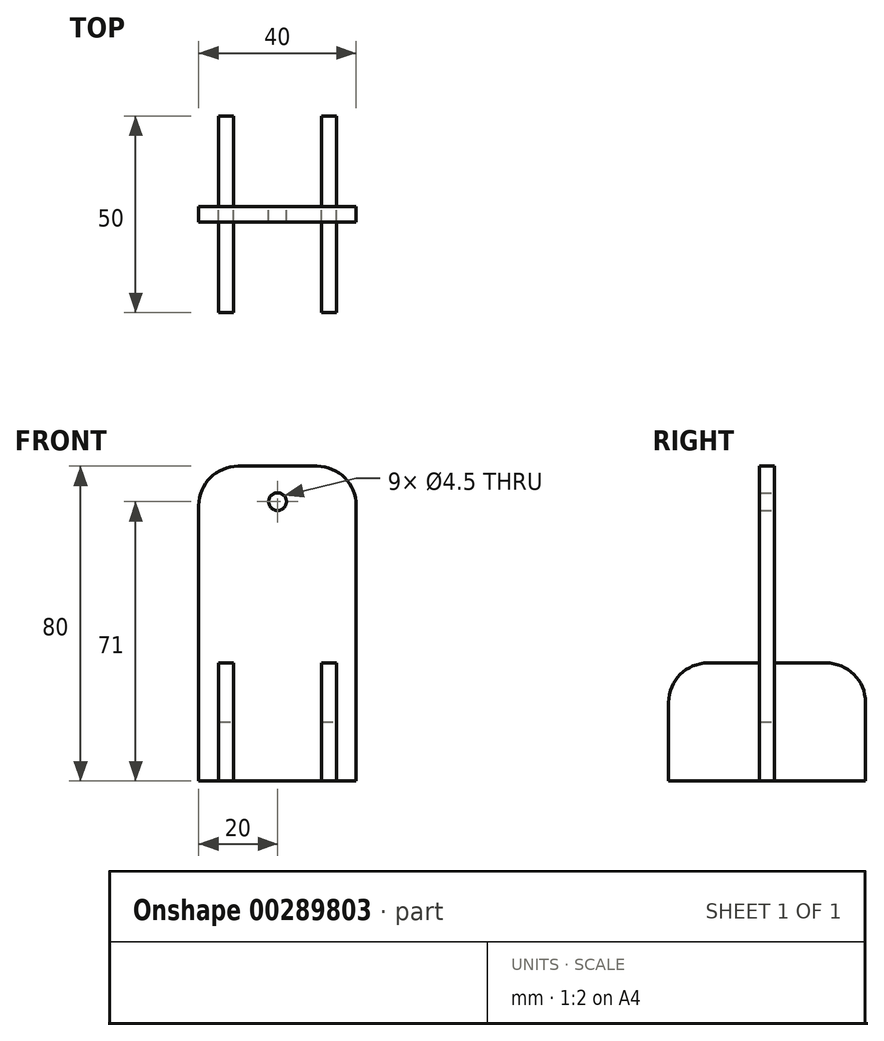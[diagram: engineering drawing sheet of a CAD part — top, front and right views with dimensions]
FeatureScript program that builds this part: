
annotation { "Feature Type Name" : "Feature", "Feature Type Description" : "" }
export const myFeature = defineFeature(function(context is Context, id is Id, definition is map)
    precondition{}
    {
        {
            var Q0;
            Q0=qCreatedBy(makeId("Front.planeOp"),FACE);
            var sketch = newSketch(context, id + "F0", { "sketchPlane" : qUnion([Q0])});
            skLineSegment(sketch, "E0.bottom", {"start": v(20, -40) * mm, "end": v(15, -40) * mm});
            skLineSegment(sketch, "E0.top", {"start": v(10, 40) * mm, "end": v(-10, 40) * mm});
            skLineSegment(sketch, "E0.left", {"start": v(20, -40) * mm, "end": v(20, 30) * mm});
            skLineSegment(sketch, "E0.right", {"start": v(-20, -40) * mm, "end": v(-20, 30) * mm});
            skPoint(sketch, "E0.middle", {"position": v(0, 0) * mm});
            skLineSegment(sketch, "E1", {"start": v(-15, -40) * mm, "end": v(-15, -25) * mm});
            skLineSegment(sketch, "E2", {"start": v(-15, -25) * mm, "end": v(-11.15, -25) * mm});
            skLineSegment(sketch, "E3", {"start": v(-11.15, -25) * mm, "end": v(-11.15, -40) * mm});
            skLineSegment(sketch, "E4", {"start": v(-11.15, -40) * mm, "end": v(11.15, -40) * mm});
            skLineSegment(sketch, "E5", {"start": v(11.15, -40) * mm, "end": v(11.15, -25) * mm});
            skLineSegment(sketch, "E6", {"start": v(11.15, -25) * mm, "end": v(15, -25) * mm});
            skLineSegment(sketch, "E7", {"start": v(15, -25) * mm, "end": v(15, -40) * mm});
            skLineSegment(sketch, "E8.trimOffspring", {"start": v(11.15, -40) * mm, "end": v(-11.15, -40) * mm});
            skLineSegment(sketch, "E9.trimOffspring", {"start": v(-15, -40) * mm, "end": v(-20, -40) * mm});
            skPoint(sketch, "E10.visualSharp", {"position": v(20, 40) * mm});
            skArc(sketch, "E10.filletArc", {"start": v(20, 30) * mm, "mid": v(17.07, 37.07) * mm, "end": v(10, 40) * mm});
            skPoint(sketch, "E11.visualSharp", {"position": v(-20, 40) * mm});
            skArc(sketch, "E11.filletArc", {"start": v(-10, 40) * mm, "mid": v(-17.07, 37.07) * mm, "end": v(-20, 30) * mm});
            skPoint(sketch, "E12", {"position": v(0, 40) * mm});
            skLineSegment(sketch, "E13", {"start": v(0, 40) * mm, "end": v(0, 31) * mm, "construction": true});
            skCircle(sketch, "E14", {"center": v(0, 31) * mm, "radius": 2.25 * mm});
            skSolve(sketch);
        }
        {
            var Q0;
            Q0 = qSketchRegion(id + "F0", true);
            extrude(context, id + "F1", {"entities" : qUnion([Q0]), "endBound" : BoundingType.SYMMETRIC, "depth" : 3.85 * mm});
        }
        {
            var Q0;
            Q0=qCreatedBy(makeId("Right.planeOp"),FACE);
            var sketch = newSketch(context, id + "F2", { "sketchPlane" : qUnion([Q0])});
            skPoint(sketch, "E15.0", {"position": v(0, -25) * mm});
            skLineSegment(sketch, "E16.bottom", {"start": v(-15, -10) * mm, "end": v(-1.92, -10) * mm});
            skLineSegment(sketch, "E16.top", {"start": v(-25, -40) * mm, "end": v(-1.93, -40) * mm});
            skLineSegment(sketch, "E16.left", {"start": v(-25, -20) * mm, "end": v(-25, -40) * mm});
            skLineSegment(sketch, "E16.right", {"start": v(25, -20) * mm, "end": v(25, -40) * mm});
            skPoint(sketch, "E17.visualSharp", {"position": v(25, -10) * mm});
            skArc(sketch, "E17.filletArc", {"start": v(25, -20) * mm, "mid": v(22.07, -12.93) * mm, "end": v(15, -10) * mm});
            skPoint(sketch, "E18.visualSharp", {"position": v(-25, -10) * mm});
            skArc(sketch, "E18.filletArc", {"start": v(-15, -10) * mm, "mid": v(-22.07, -12.93) * mm, "end": v(-25, -20) * mm});
            skPoint(sketch, "E19.0.11.end.orphan", {"position": v(0, -40) * mm});
            skPoint(sketch, "E19.0.7.start.orphan", {"position": v(0, 30) * mm});
            skPoint(sketch, "E19.0.5.start.orphan", {"position": v(0, -40) * mm});
            skPoint(sketch, "E19.0.9.start.orphan", {"position": v(0, -40) * mm});
            skPoint(sketch, "E19.0.3.end.orphan", {"position": v(0, -40) * mm});
            skPoint(sketch, "E19.0.1.start.orphan", {"position": v(0, -40) * mm});
            skLineSegment(sketch, "E20.0.0", {"start": v(1.93, -10) * mm, "end": v(1.93, -25) * mm});
            skLineSegment(sketch, "E20.0.1", {"start": v(1.93, -40) * mm, "end": v(-1.93, -40) * mm});
            skLineSegment(sketch, "E20.0.2", {"start": v(-1.93, -25) * mm, "end": v(-1.93, -10) * mm});
            skLineSegment(sketch, "E20.0.3", {"start": v(-1.93, 30) * mm, "end": v(1.92, 30) * mm});
            skLineSegment(sketch, "E21.0", {"start": v(-1.93, -25) * mm, "end": v(1.92, -25) * mm});
            skLineSegment(sketch, "E22.trimOffspring", {"start": v(1.93, -40) * mm, "end": v(25, -40) * mm});
            skLineSegment(sketch, "E23.trimOffspring", {"start": v(1.92, -10) * mm, "end": v(15, -10) * mm});
            skSolve(sketch);
        }
        {
            var Q0;
            Q0=makeQuery(id+"F1.opExtrude","SWEPT_FACE",FACE,{"disambiguationData":[OSD([sQuery(id+"F0.wireOp",EDGE,"E3")])]});
            var sketch = newSketch(context, id + "F3", { "sketchPlane" : qUnion([Q0])});
            skLineSegment(sketch, "E24.0.0", {"start": v(-25, -40) * mm, "end": v(-25, -20) * mm});
            skArc(sketch, "E24.0.1", {"start": v(-25, -20) * mm, "mid": v(-22.07, -12.93) * mm, "end": v(-15, -10) * mm});
            skLineSegment(sketch, "E24.0.2", {"start": v(-15, -10) * mm, "end": v(-1.92, -10) * mm});
            skLineSegment(sketch, "E24.0.3", {"start": v(-1.93, -10) * mm, "end": v(-1.93, -25) * mm});
            skLineSegment(sketch, "E24.0.4", {"start": v(-1.93, -25) * mm, "end": v(1.93, -25) * mm});
            skLineSegment(sketch, "E24.0.5", {"start": v(1.93, -25) * mm, "end": v(1.93, -10) * mm});
            skLineSegment(sketch, "E24.0.6", {"start": v(1.92, -10) * mm, "end": v(15, -10) * mm});
            skArc(sketch, "E24.0.7", {"start": v(15, -10) * mm, "mid": v(22.07, -12.93) * mm, "end": v(25, -20) * mm});
            skLineSegment(sketch, "E24.0.8", {"start": v(25, -20) * mm, "end": v(25, -40) * mm});
            skLineSegment(sketch, "E24.0.9", {"start": v(25, -40) * mm, "end": v(1.93, -40) * mm});
            skLineSegment(sketch, "E24.0.10", {"start": v(1.93, -40) * mm, "end": v(-1.93, -40) * mm});
            skLineSegment(sketch, "E24.0.11", {"start": v(-1.93, -40) * mm, "end": v(-25, -40) * mm});
            skSolve(sketch);
        }
        {
            var Q0;
            Q0=makeQuery(id+"F1.opExtrude","SWEPT_FACE",FACE,{"disambiguationData":[OSD([sQuery(id+"F0.wireOp",EDGE,"E5")])]});
            var sketch = newSketch(context, id + "F4", { "sketchPlane" : qUnion([Q0])});
            skLineSegment(sketch, "E25.0.0", {"start": v(25, -40) * mm, "end": v(25, -20) * mm});
            skArc(sketch, "E25.0.1", {"start": v(25, -20) * mm, "mid": v(22.07, -12.93) * mm, "end": v(15, -10) * mm});
            skLineSegment(sketch, "E25.0.2", {"start": v(15, -10) * mm, "end": v(1.92, -10) * mm});
            skLineSegment(sketch, "E25.0.3", {"start": v(1.93, -10) * mm, "end": v(1.93, -25) * mm});
            skLineSegment(sketch, "E25.0.4", {"start": v(1.93, -25) * mm, "end": v(-1.93, -25) * mm});
            skLineSegment(sketch, "E25.0.5", {"start": v(-1.93, -25) * mm, "end": v(-1.93, -10) * mm});
            skLineSegment(sketch, "E25.0.6", {"start": v(-1.92, -10) * mm, "end": v(-15, -10) * mm});
            skArc(sketch, "E25.0.7", {"start": v(-15, -10) * mm, "mid": v(-22.07, -12.93) * mm, "end": v(-25, -20) * mm});
            skLineSegment(sketch, "E25.0.8", {"start": v(-25, -20) * mm, "end": v(-25, -40) * mm});
            skLineSegment(sketch, "E25.0.9", {"start": v(-25, -40) * mm, "end": v(-1.93, -40) * mm});
            skLineSegment(sketch, "E25.0.10", {"start": v(-1.93, -40) * mm, "end": v(1.93, -40) * mm});
            skLineSegment(sketch, "E25.0.11", {"start": v(1.93, -40) * mm, "end": v(25, -40) * mm});
            skSolve(sketch);
        }
        {
            var Q0;
            Q0 = qSketchRegion(id + "F3", true);
            var Q1;
            Q1=makeQuery(id+"F1.opExtrude","SWEPT_FACE",FACE,{"disambiguationData":[OSD([sQuery(id+"F0.wireOp",EDGE,"E1")])]});
            extrude(context, id + "F5", {"entities" : qUnion([Q0]), "endBound" : BoundingType.UP_TO_SURFACE, "endBoundEntityFace" : qUnion([Q1]), "depth" : 25 * mm});
        }
        {
            var Q0;
            Q0 = qSketchRegion(id + "F4", true);
            var Q1;
            Q1=makeQuery(id+"F1.opExtrude","SWEPT_FACE",FACE,{"disambiguationData":[OSD([sQuery(id+"F0.wireOp",EDGE,"E7")])]});
            extrude(context, id + "F6", {"entities" : qUnion([Q0]), "endBound" : BoundingType.UP_TO_SURFACE, "endBoundEntityFace" : qUnion([Q1]), "depth" : 25 * mm});
        }
    });
